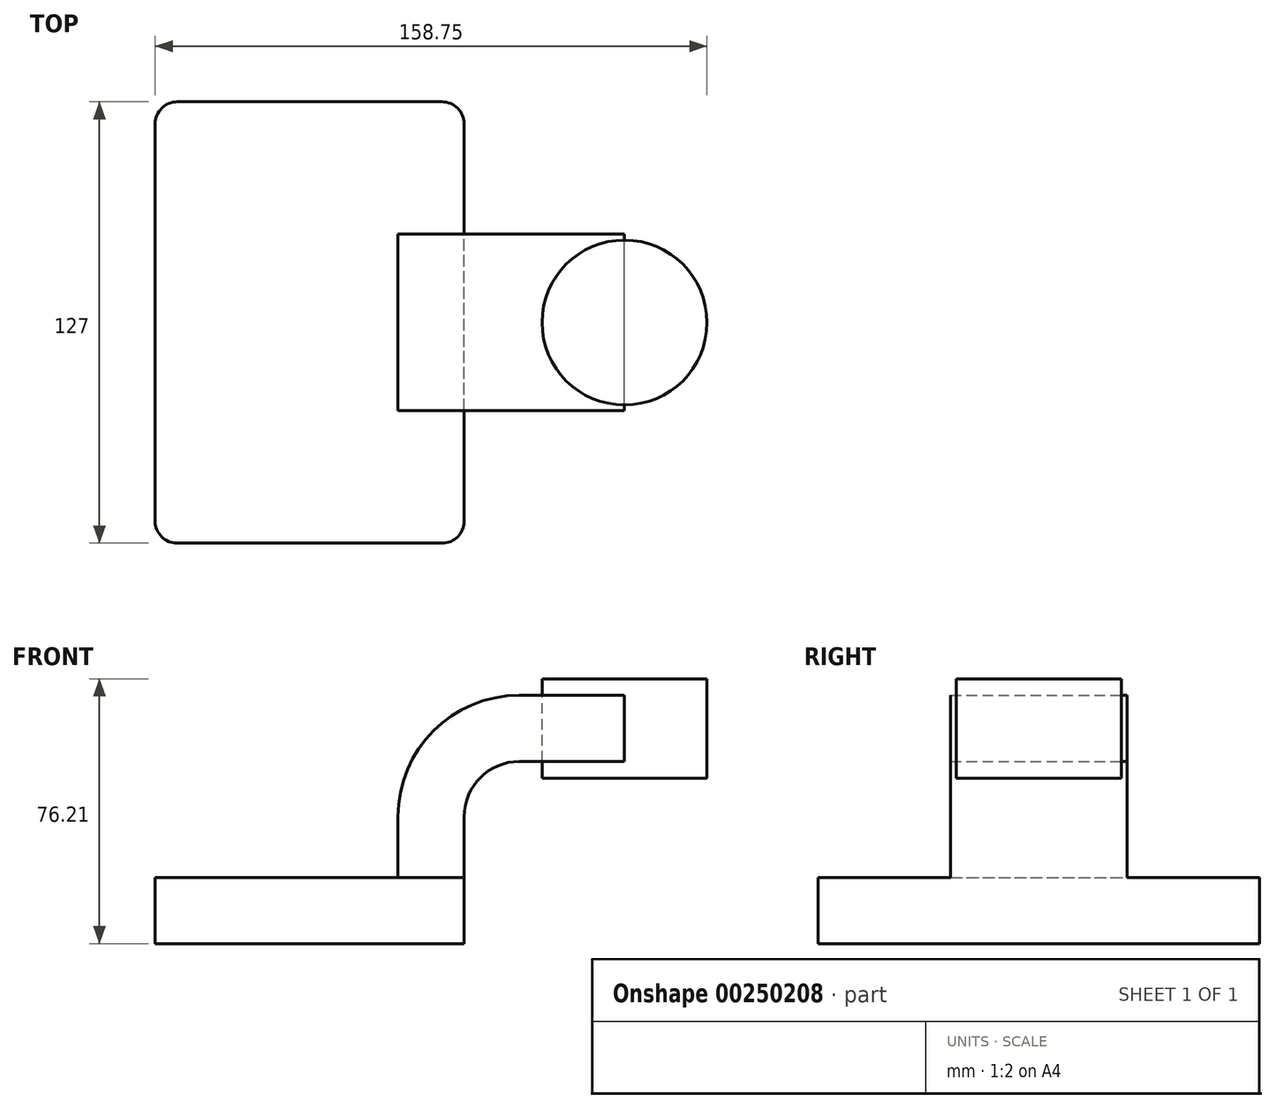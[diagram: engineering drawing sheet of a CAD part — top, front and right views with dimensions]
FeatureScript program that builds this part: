
annotation { "Feature Type Name" : "Feature", "Feature Type Description" : "" }
export const myFeature = defineFeature(function(context is Context, id is Id, definition is map)
    precondition{}
    {
        {
            var Q0;
            Q0=qCreatedBy(makeId("Front.planeOp"),FACE);
            var sketch = newSketch(context, id + "F0", { "sketchPlane" : qUnion([Q0])});
            skLineSegment(sketch, "E0.bottom", {"start": v(44.45, -9.52) * mm, "end": v(-44.45, -9.53) * mm});
            skLineSegment(sketch, "E0.top", {"start": v(44.45, 9.53) * mm, "end": v(-44.45, 9.53) * mm});
            skLineSegment(sketch, "E0.left", {"start": v(44.45, -9.52) * mm, "end": v(44.45, 9.53) * mm});
            skLineSegment(sketch, "E0.right", {"start": v(-44.45, -9.52) * mm, "end": v(-44.45, 9.53) * mm});
            skPoint(sketch, "E0.middle", {"position": v(0, 0) * mm});
            skLineSegment(sketch, "E1.bottom", {"start": v(114.3, 66.68) * mm, "end": v(63.5, 66.68) * mm});
            skLineSegment(sketch, "E1.top", {"start": v(114.3, 38.1) * mm, "end": v(63.5, 38.1) * mm});
            skLineSegment(sketch, "E1.left", {"start": v(63.5, 38.1) * mm, "end": v(63.5, 66.67) * mm});
            skLineSegment(sketch, "E1.right", {"start": v(114.3, 38.1) * mm, "end": v(114.3, 66.67) * mm});
            skPoint(sketch, "E1.middle", {"position": v(88.9, 52.39) * mm});
            skLineSegment(sketch, "E2", {"start": v(44.45, 9.53) * mm, "end": v(44.45, 27) * mm});
            skArc(sketch, "E3", {"start": v(44.45, 27) * mm, "mid": v(49.1, 38.23) * mm, "end": v(60.32, 42.88) * mm});
            skLineSegment(sketch, "E4", {"start": v(60.32, 42.88) * mm, "end": v(90.58, 42.88) * mm});
            skLineSegment(sketch, "E5.0", {"start": v(60.32, 61.93) * mm, "end": v(90.58, 61.93) * mm});
            skArc(sketch, "E5.1", {"start": v(25.4, 27) * mm, "mid": v(35.63, 51.7) * mm, "end": v(60.32, 61.93) * mm});
            skLineSegment(sketch, "E5.2", {"start": v(25.4, 9.53) * mm, "end": v(25.4, 27) * mm});
            skLineSegment(sketch, "E6", {"start": v(90.58, 66.68) * mm, "end": v(90.58, 38.1) * mm});
            skPoint(sketch, "E6.endSnap0", {"position": v(88.9, 38.1) * mm});
            skFitSpline(sketch, "E7", {"points": [v(-44.45, 9.52) * mm, v(60.32, 61.93) * mm], "startDerivative": vector(0, 70.35) * mm, "endDerivative": vector(195.1, 0) * mm});
            skSolve(sketch);
        }
        {
            var Q0;
            Q0=makeQuery(id+"F0.imprint","IMPRINT",FACE,{"disambiguationData":[TD([[makeQuery(id+"F0.imprint","IMPRINT",EDGE,{"derivedFrom":sQuery(id+"F0.wireOp",EDGE,"E0.bottom")}),-1.0]])]});
            extrude(context, id + "F1", {"entities" : qUnion([Q0]), "endBound" : BoundingType.SYMMETRIC, "depth" : 127 * mm});
        }
        {
            var Q0;
            {var subQ1=sQuery(id+"F0.wireOp",EDGE,"E2");Q0=makeQuery(id+"F0.imprint","IMPRINT",FACE,{"disambiguationData":[TD([[makeQuery(id+"F0.imprint","IMPRINT",EDGE,{"derivedFrom":subQ1}),1.0]])]});}
            var Q1;
            {var subQ0=sQuery(id+"F0.wireOp",EDGE,"E4");var subQ1=sQuery(id+"F0.wireOp",EDGE,"E1.left");var subQ2=makeQuery(id+"F0.imprint","INTERSECT",VERTEX,{"derivedFrom":[subQ1,subQ0]});Q1=makeQuery(id+"F0.imprint","IMPRINT",FACE,{"disambiguationData":[TD([[makeQuery(id+"F0.imprint","IMPRINT",EDGE,{"disambiguationData":[TD([[subQ2,-1.0]])],"derivedFrom":subQ1}),-1.0]])]});}
            extrude(context, id + "F2", {"entities" : qUnion([Q0, Q1]), "operationType" : NewBodyOperationType.ADD, "endBound" : BoundingType.SYMMETRIC, "depth" : 50.8 * mm});
        }
        {
            var Q0;
            Q0=makeQuery(id+"F0.imprint","IMPRINT",FACE,{"disambiguationData":[TD([[makeQuery(id+"F0.imprint","IMPRINT",EDGE,{"derivedFrom":sQuery(id+"F0.wireOp",EDGE,"E5.1")}),1.0]])]});
            extrude(context, id + "F3", {"entities" : qUnion([Q0]), "operationType" : NewBodyOperationType.ADD, "endBound" : BoundingType.SYMMETRIC, "depth" : 15.88 * mm});
        }
        {
            var Q0;
            {var subQ0=sQuery(id+"F0.wireOp",EDGE,"E1.right");Q0=makeQuery(id+"F0.imprint","IMPRINT",FACE,{"disambiguationData":[TD([[makeQuery(id+"F0.imprint","IMPRINT",EDGE,{"derivedFrom":subQ0}),1.0]])]});}
            var Q1;
            Q1=sQuery(id+"F0.wireOp",EDGE,"E6");
            revolve(context, id + "F4", {"entities" : qUnion([Q0]), "axis" : qUnion([Q1]), "revolveType" : RevolveType.FULL});
        }
        {
            var Q0;
            Q0=makeQuery(id+"F1.opExtrude","CAP_EDGE",EDGE,{"disambiguationData":[OSD([sQuery(id+"F0.wireOp",EDGE,"E0.left")])],"isStart":false});
            var Q1;
            Q1=makeQuery(id+"F1.opExtrude","CAP_EDGE",EDGE,{"disambiguationData":[OSD([sQuery(id+"F0.wireOp",EDGE,"E0.right")])],"isStart":false});
            var Q2;
            Q2=makeQuery(id+"F1.opExtrude","CAP_EDGE",EDGE,{"disambiguationData":[OSD([sQuery(id+"F0.wireOp",EDGE,"E0.left")])],"isStart":true});
            var Q3;
            Q3=makeQuery(id+"F1.opExtrude","CAP_EDGE",EDGE,{"disambiguationData":[OSD([sQuery(id+"F0.wireOp",EDGE,"E0.right")])],"isStart":true});
            fillet(context, id + "F5", {"entities" : qUnion([Q0, Q1, Q2, Q3]), "radius" : 6.35 * mm, "tangentPropagation" : true, "allowEdgeOverflow" : false});
        }
    });
